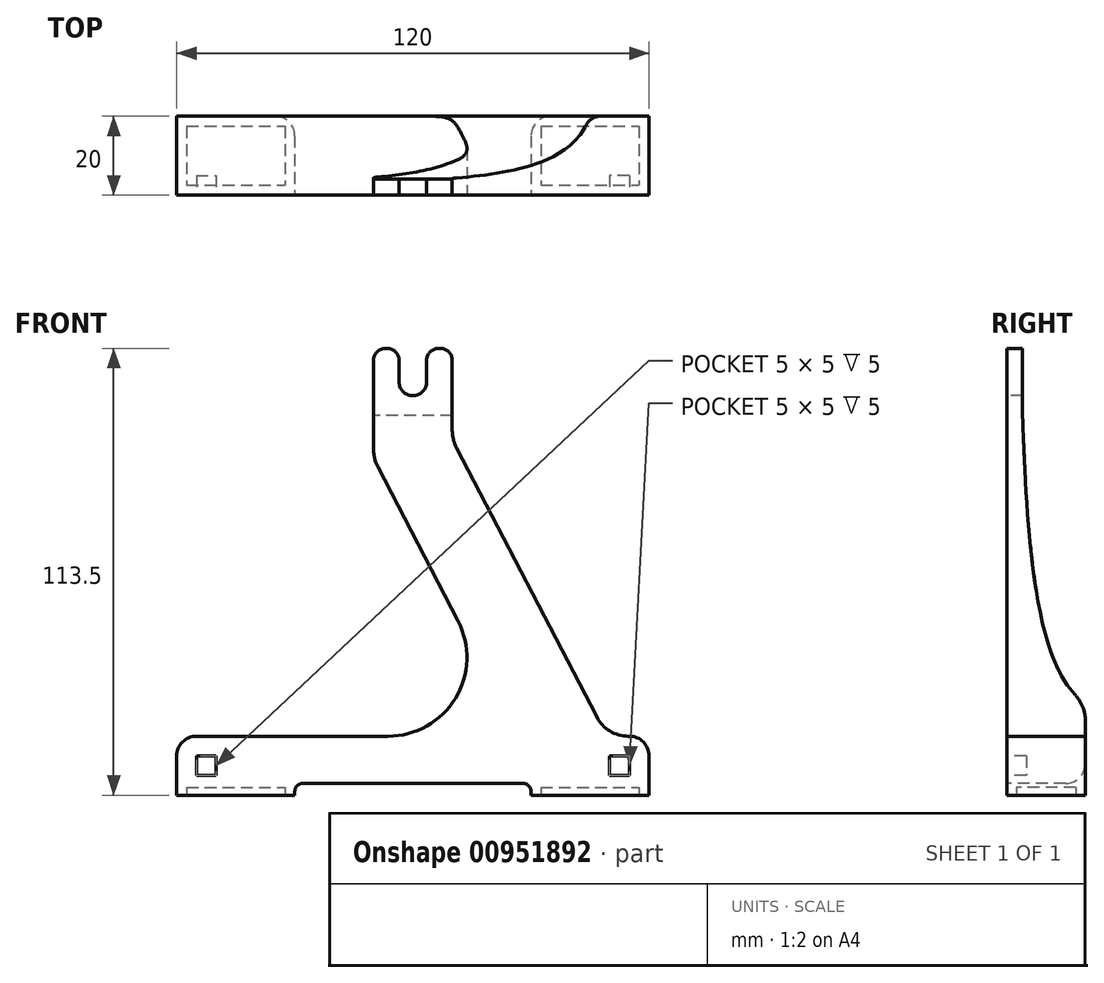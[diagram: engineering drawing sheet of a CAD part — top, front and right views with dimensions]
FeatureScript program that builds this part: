
annotation { "Feature Type Name" : "Feature", "Feature Type Description" : "" }
export const myFeature = defineFeature(function(context is Context, id is Id, definition is map)
    precondition{}
    {
        {
            var Q0;
            Q0=qCreatedBy(makeId("Front.planeOp"),FACE);
            var sketch = newSketch(context, id + "F0", { "sketchPlane" : qUnion([Q0])});
            skArc(sketch, "E0", {"start": v(-3.5, 105) * mm, "mid": v(0, 101.5) * mm, "end": v(3.5, 105) * mm});
            skCircle(sketch, "E1", {"center": v(0, 105) * mm, "radius": 100 * mm, "construction": true});
            skLineSegment(sketch, "E2", {"start": v(-10, 110.5) * mm, "end": v(-10, 87.96) * mm});
            skLineSegment(sketch, "E3", {"start": v(-20, 15) * mm, "end": v(-55, 15) * mm});
            skLineSegment(sketch, "E4", {"start": v(-60, 10) * mm, "end": v(-60, 0) * mm});
            skLineSegment(sketch, "E5", {"start": v(-60, 0) * mm, "end": v(-30, 0) * mm});
            skLineSegment(sketch, "E6", {"start": v(-28, 3) * mm, "end": v(28, 3) * mm});
            skLineSegment(sketch, "E7", {"start": v(30, 0) * mm, "end": v(60, 0) * mm});
            skLineSegment(sketch, "E8", {"start": v(60, 0) * mm, "end": v(60, 10) * mm});
            skLineSegment(sketch, "E9", {"start": v(55, 15) * mm, "end": v(54.7, 15) * mm});
            skLineSegment(sketch, "E10", {"start": v(10, 92.85) * mm, "end": v(10, 110.5) * mm});
            skLineSegment(sketch, "E11", {"start": v(7, 113.5) * mm, "end": v(6.5, 113.5) * mm});
            skLineSegment(sketch, "E12", {"start": v(-30, 1) * mm, "end": v(-30, 0) * mm});
            skLineSegment(sketch, "E13", {"start": v(30, 1) * mm, "end": v(30, 0) * mm});
            skPoint(sketch, "E14.orphan", {"position": v(-45, 0) * mm});
            skPoint(sketch, "E15.orphan", {"position": v(45, 0) * mm});
            skPoint(sketch, "E16.visualSharp", {"position": v(-10, 15) * mm});
            skPoint(sketch, "E17.visualSharp", {"position": v(10, 15) * mm});
            skPoint(sketch, "E18.visualSharp", {"position": v(-10, 113.5) * mm});
            skArc(sketch, "E18.filletArc", {"start": v(-7, 113.5) * mm, "mid": v(-9.12, 112.62) * mm, "end": v(-10, 110.5) * mm});
            skPoint(sketch, "E19.visualSharp", {"position": v(10, 113.5) * mm});
            skArc(sketch, "E19.filletArc", {"start": v(10, 110.5) * mm, "mid": v(9.12, 112.62) * mm, "end": v(7, 113.5) * mm});
            skPoint(sketch, "E20.visualSharp", {"position": v(-60, 15) * mm});
            skArc(sketch, "E20.filletArc", {"start": v(-55, 15) * mm, "mid": v(-58.54, 13.54) * mm, "end": v(-60, 10) * mm});
            skPoint(sketch, "E21.visualSharp", {"position": v(60, 15) * mm});
            skArc(sketch, "E21.filletArc", {"start": v(60, 10) * mm, "mid": v(58.54, 13.54) * mm, "end": v(55, 15) * mm});
            skPoint(sketch, "E22.visualSharp", {"position": v(30, 3) * mm});
            skArc(sketch, "E22.filletArc", {"start": v(30, 1) * mm, "mid": v(29.41, 2.41) * mm, "end": v(28, 3) * mm});
            skPoint(sketch, "E23.visualSharp", {"position": v(-30, 3) * mm});
            skArc(sketch, "E23.filletArc", {"start": v(-28, 3) * mm, "mid": v(-29.41, 2.41) * mm, "end": v(-30, 1) * mm});
            skLineSegment(sketch, "E24", {"start": v(-3.5, 105) * mm, "end": v(-3.5, 110.5) * mm});
            skLineSegment(sketch, "E25", {"start": v(3.5, 105) * mm, "end": v(3.5, 110.5) * mm});
            skLineSegment(sketch, "E26.trimOffspring", {"start": v(-6.5, 113.5) * mm, "end": v(-7, 113.5) * mm});
            skPoint(sketch, "E27.visualSharp", {"position": v(-3.5, 113.5) * mm});
            skArc(sketch, "E27.filletArc", {"start": v(-3.5, 110.5) * mm, "mid": v(-4.38, 112.62) * mm, "end": v(-6.5, 113.5) * mm});
            skPoint(sketch, "E28.visualSharp", {"position": v(3.5, 113.5) * mm});
            skArc(sketch, "E28.filletArc", {"start": v(6.5, 113.5) * mm, "mid": v(4.38, 112.62) * mm, "end": v(3.5, 110.5) * mm});
            skLineSegment(sketch, "E29", {"start": v(11.13, 88.23) * mm, "end": v(46.72, 19.85) * mm});
            skLineSegment(sketch, "E30", {"start": v(-8.87, 83.34) * mm, "end": v(11.48, 44.23) * mm});
            skLineSegment(sketch, "E31.trimOffspring", {"start": v(-6.26, 15) * mm, "end": v(-20, 15) * mm});
            skPoint(sketch, "E32.visualSharp", {"position": v(-10, 85.5) * mm});
            skArc(sketch, "E32.filletArc", {"start": v(-10, 87.96) * mm, "mid": v(-9.71, 85.58) * mm, "end": v(-8.87, 83.34) * mm});
            skPoint(sketch, "E33.visualSharp", {"position": v(10, 90.4) * mm});
            skArc(sketch, "E33.filletArc", {"start": v(10, 92.85) * mm, "mid": v(10.29, 90.47) * mm, "end": v(11.13, 88.23) * mm});
            skPoint(sketch, "E34.visualSharp", {"position": v(49.24, 15) * mm});
            skArc(sketch, "E34.filletArc", {"start": v(46.72, 19.85) * mm, "mid": v(50.03, 16.3) * mm, "end": v(54.7, 15) * mm});
            skPoint(sketch, "E35.visualSharp", {"position": v(26.7, 15) * mm});
            skArc(sketch, "E35.filletArc", {"start": v(-6.26, 15) * mm, "mid": v(10.84, 24.62) * mm, "end": v(11.48, 44.23) * mm});
            skSolve(sketch);
        }
        {
            var Q0;
            Q0=makeQuery(id+"F0.imprint","IMPRINT",FACE,{"disambiguationData":[TD([[makeQuery(id+"F0.imprint","IMPRINT",EDGE,{"derivedFrom":sQuery(id+"F0.wireOp",EDGE,"E0")}),-1.0]])]});
            extrude(context, id + "F1", {"entities" : qUnion([Q0]), "depth" : 20 * mm, "offsetDistance" : 25 * mm});
        }
        {
            var Q0;
            Q0=makeQuery(id+"F1.opExtrude","SWEPT_FACE",FACE,{"disambiguationData":[OSD([sQuery(id+"F0.wireOp",EDGE,"E10")])]});
            var sketch = newSketch(context, id + "F2", { "sketchPlane" : qUnion([Q0])});
            skLineSegment(sketch, "E36", {"start": v(-4, 116.6) * mm, "end": v(-4, 96.5) * mm});
            skLineSegment(sketch, "E37", {"start": v(-20, 116.6) * mm, "end": v(-4, 116.6) * mm});
            skPoint(sketch, "E38.visualSharp", {"position": v(-4, 88.5) * mm});
            skLineSegment(sketch, "E39", {"start": v(-25.17, 79.44) * mm, "end": v(-25.17, 116.6) * mm});
            skLineSegment(sketch, "E40", {"start": v(-25.17, 116.6) * mm, "end": v(-20, 116.6) * mm});
            skPoint(sketch, "E41.visualSharp", {"position": v(-20, 88.5) * mm});
            skFitSpline(sketch, "E42", {"points": [v(-4, 96.5) * mm, v(-13.32, 31.43) * mm, v(-22.33, 23.5) * mm, v(-25.17, 79.44) * mm], "startDerivative": vector(-7.01, -189.31) * mm, "endDerivative": vector(0.02, 210.5) * mm});
            skSolve(sketch);
        }
        {
            var Q0;
            Q0=makeQuery(id+"F1.opExtrude","SWEPT_FACE",FACE,{"disambiguationData":[OSD([sQuery(id+"F0.wireOp",EDGE,"E5")])]});
            var sketch = newSketch(context, id + "F3", { "sketchPlane" : qUnion([Q0])});
            skLineSegment(sketch, "E43.bottom", {"start": v(-57.5, 17.5) * mm, "end": v(-32.5, 17.5) * mm});
            skLineSegment(sketch, "E43.top", {"start": v(-57.5, 2.5) * mm, "end": v(-32.5, 2.5) * mm});
            skLineSegment(sketch, "E43.left", {"start": v(-57.5, 17.5) * mm, "end": v(-57.5, 2.5) * mm});
            skLineSegment(sketch, "E43.right", {"start": v(-32.5, 17.5) * mm, "end": v(-32.5, 2.5) * mm});
            skLineSegment(sketch, "E44.bottom", {"start": v(32.5, 17.5) * mm, "end": v(57.5, 17.5) * mm});
            skLineSegment(sketch, "E44.top", {"start": v(32.5, 2.5) * mm, "end": v(57.5, 2.5) * mm});
            skLineSegment(sketch, "E44.left", {"start": v(32.5, 17.5) * mm, "end": v(32.5, 2.5) * mm});
            skLineSegment(sketch, "E44.right", {"start": v(57.5, 17.5) * mm, "end": v(57.5, 2.5) * mm});
            skSolve(sketch);
        }
        {
            var Q0;
            Q0=makeQuery(id+"F3.imprint","IMPRINT",FACE,{"disambiguationData":[TD([[makeQuery(id+"F3.imprint","IMPRINT",EDGE,{"derivedFrom":sQuery(id+"F3.wireOp",EDGE,"E43.bottom")}),-1.0]])]});
            var Q1;
            Q1=makeQuery(id+"F3.imprint","IMPRINT",FACE,{"disambiguationData":[TD([[makeQuery(id+"F3.imprint","IMPRINT",EDGE,{"derivedFrom":sQuery(id+"F3.wireOp",EDGE,"E44.bottom")}),-1.0]])]});
            extrude(context, id + "F4", {"entities" : qUnion([Q0, Q1]), "operationType" : NewBodyOperationType.REMOVE, "oppositeDirection" : true, "depth" : 2 * mm, "offsetDistance" : 25 * mm});
        }
        {
            var Q0;
            {var subQ1=sQuery(id+"F2.wireOp",EDGE,"E37");Q0=makeQuery(id+"F2.imprint","IMPRINT",FACE,{"disambiguationData":[TD([[makeQuery(id+"F2.imprint","IMPRINT",EDGE,{"derivedFrom":subQ1}),-1.0]])]});}
            var Q1;
            {var subQ0=sQuery(id+"F0.wireOp",EDGE,"E10");var subQ1=makeQuery(id+"F1.opExtrude","CAP_EDGE",EDGE,{"disambiguationData":[OSD([subQ0])],"isStart":false});Q1=makeQuery(id+"F2.imprint","IMPRINT",FACE,{"disambiguationData":[TD([[makeQuery(id+"F2.imprint","IMPRINT",EDGE,{"derivedFrom":subQ1}),-1.0]])]});}
            extrude(context, id + "F5", {"entities" : qUnion([Q0, Q1]), "operationType" : NewBodyOperationType.REMOVE, "depth" : 75 * mm, "offsetDistance" : 25 * mm, "symmetric" : true});
        }
        {
            var Q0;
            Q0=makeQuery(id+"F5.boolean.opBoolean","INTERSECT",EDGE,{"derivedFrom":[makeQuery(id+"F1.opExtrude","CAP_FACE",FACE,{"disambiguationData":[OSD([sQuery(id+"F0.wireOp",EDGE,"E0"),sQuery(id+"F0.wireOp",EDGE,"E2"),sQuery(id+"F0.wireOp",EDGE,"E3"),sQuery(id+"F0.wireOp",EDGE,"E4"),sQuery(id+"F0.wireOp",EDGE,"E5"),sQuery(id+"F0.wireOp",EDGE,"E6"),sQuery(id+"F0.wireOp",EDGE,"E7"),sQuery(id+"F0.wireOp",EDGE,"E8"),sQuery(id+"F0.wireOp",EDGE,"E9"),sQuery(id+"F0.wireOp",EDGE,"E10"),sQuery(id+"F0.wireOp",EDGE,"E11"),sQuery(id+"F0.wireOp",EDGE,"E12"),sQuery(id+"F0.wireOp",EDGE,"E13"),sQuery(id+"F0.wireOp",EDGE,"E18.filletArc"),sQuery(id+"F0.wireOp",EDGE,"E19.filletArc"),sQuery(id+"F0.wireOp",EDGE,"E20.filletArc"),sQuery(id+"F0.wireOp",EDGE,"E21.filletArc"),sQuery(id+"F0.wireOp",EDGE,"E22.filletArc"),sQuery(id+"F0.wireOp",EDGE,"E23.filletArc"),sQuery(id+"F0.wireOp",EDGE,"E24"),sQuery(id+"F0.wireOp",EDGE,"E25"),sQuery(id+"F0.wireOp",EDGE,"E26.trimOffspring"),sQuery(id+"F0.wireOp",EDGE,"E27.filletArc"),sQuery(id+"F0.wireOp",EDGE,"E28.filletArc"),sQuery(id+"F0.wireOp",EDGE,"E29"),sQuery(id+"F0.wireOp",EDGE,"E30"),sQuery(id+"F0.wireOp",EDGE,"E31.trimOffspring"),sQuery(id+"F0.wireOp",EDGE,"E32.filletArc"),sQuery(id+"F0.wireOp",EDGE,"E33.filletArc"),sQuery(id+"F0.wireOp",EDGE,"E34.filletArc"),sQuery(id+"F0.wireOp",EDGE,"E35.filletArc")])],"isStart":false}),makeQuery(id+"F5.opExtrude","SWEPT_FACE",FACE,{"disambiguationData":[OSD([sQuery(id+"F2.wireOp",EDGE,"E42")])]})]});
            fillet(context, id + "F6", {"entities" : qUnion([Q0]), "radius" : 10 * mm, "tangentPropagation" : true, "allowEdgeOverflow" : false});
        }
        {
            var Q0;
            Q0=makeQuery(id+"F1.opExtrude","CAP_EDGE",EDGE,{"disambiguationData":[OSD([sQuery(id+"F0.wireOp",EDGE,"E6")])],"isStart":false});
            fillet(context, id + "F7", {"entities" : qUnion([Q0]), "radius" : 5 * mm, "tangentPropagation" : true, "allowEdgeOverflow" : false});
        }
        {
            var Q0;
            Q0=makeQuery(id+"F0.imprint","IMPRINT",FACE,{"disambiguationData":[TD([[makeQuery(id+"F0.imprint","IMPRINT",EDGE,{"derivedFrom":sQuery(id+"F0.wireOp",EDGE,"E0")}),-1.0]])]});
            var sketch = newSketch(context, id + "F8", { "sketchPlane" : qUnion([Q0])});
            skLineSegment(sketch, "E45.bottom", {"start": v(55, 10) * mm, "end": v(50, 10) * mm});
            skLineSegment(sketch, "E45.top", {"start": v(55, 5) * mm, "end": v(50, 5) * mm});
            skLineSegment(sketch, "E45.left", {"start": v(55, 10) * mm, "end": v(55, 5) * mm});
            skLineSegment(sketch, "E45.right", {"start": v(50, 10) * mm, "end": v(50, 5) * mm});
            skLineSegment(sketch, "E46.bottom", {"start": v(-55, 10) * mm, "end": v(-50, 10) * mm});
            skLineSegment(sketch, "E46.top", {"start": v(-55, 5) * mm, "end": v(-50, 5) * mm});
            skLineSegment(sketch, "E46.left", {"start": v(-55, 10) * mm, "end": v(-55, 5) * mm});
            skLineSegment(sketch, "E46.right", {"start": v(-50, 10) * mm, "end": v(-50, 5) * mm});
            skSolve(sketch);
        }
        {
            var Q0;
            Q0=makeQuery(id+"F8.imprint","IMPRINT",FACE,{"disambiguationData":[TD([[makeQuery(id+"F8.imprint","IMPRINT",EDGE,{"derivedFrom":sQuery(id+"F8.wireOp",EDGE,"E45.bottom")}),1.0]])]});
            var Q1;
            Q1=makeQuery(id+"F8.imprint","IMPRINT",FACE,{"disambiguationData":[TD([[makeQuery(id+"F8.imprint","IMPRINT",EDGE,{"derivedFrom":sQuery(id+"F8.wireOp",EDGE,"E46.bottom")}),-1.0]])]});
            extrude(context, id + "F9", {"entities" : qUnion([Q0, Q1]), "operationType" : NewBodyOperationType.REMOVE, "depth" : 5 * mm, "offsetDistance" : 25 * mm});
        }
        {
            var Q0;
            Q0=qCreatedBy(makeId("Front.planeOp"),FACE);
            cPlane(context, id + "F10", {"entities" : qUnion([Q0]), "cplaneType" : CPlaneType.OFFSET, "offset" : 25 * mm, "oppositeDirection" : true, "width" : 150 * mm, "height" : 150 * mm});
        }
        {
            var Q0;
            Q0=makeQuery(id+"F1.opExtrude","SWEPT_BODY",BODY,{"disambiguationData":[OSD([sQuery(id+"F0.wireOp",EDGE,"E0"),sQuery(id+"F0.wireOp",EDGE,"E2"),sQuery(id+"F0.wireOp",EDGE,"E3"),sQuery(id+"F0.wireOp",EDGE,"E4"),sQuery(id+"F0.wireOp",EDGE,"E5"),sQuery(id+"F0.wireOp",EDGE,"E6"),sQuery(id+"F0.wireOp",EDGE,"E7"),sQuery(id+"F0.wireOp",EDGE,"E8"),sQuery(id+"F0.wireOp",EDGE,"E9"),sQuery(id+"F0.wireOp",EDGE,"E10"),sQuery(id+"F0.wireOp",EDGE,"E11"),sQuery(id+"F0.wireOp",EDGE,"E12"),sQuery(id+"F0.wireOp",EDGE,"E13"),sQuery(id+"F0.wireOp",EDGE,"E18.filletArc"),sQuery(id+"F0.wireOp",EDGE,"E19.filletArc"),sQuery(id+"F0.wireOp",EDGE,"E20.filletArc"),sQuery(id+"F0.wireOp",EDGE,"E21.filletArc"),sQuery(id+"F0.wireOp",EDGE,"E22.filletArc"),sQuery(id+"F0.wireOp",EDGE,"E23.filletArc"),sQuery(id+"F0.wireOp",EDGE,"E24"),sQuery(id+"F0.wireOp",EDGE,"E25"),sQuery(id+"F0.wireOp",EDGE,"E26.trimOffspring"),sQuery(id+"F0.wireOp",EDGE,"E27.filletArc"),sQuery(id+"F0.wireOp",EDGE,"E28.filletArc"),sQuery(id+"F0.wireOp",EDGE,"E29"),sQuery(id+"F0.wireOp",EDGE,"E30"),sQuery(id+"F0.wireOp",EDGE,"E31.trimOffspring"),sQuery(id+"F0.wireOp",EDGE,"E32.filletArc"),sQuery(id+"F0.wireOp",EDGE,"E33.filletArc"),sQuery(id+"F0.wireOp",EDGE,"E34.filletArc"),sQuery(id+"F0.wireOp",EDGE,"E35.filletArc")])]});
            var Q1;
            Q1=qCreatedBy(id+"F10.planeOp",FACE);
            mirror(context, id + "F11", {"entities" : qUnion([Q0]), "mirrorPlane" : qUnion([Q1])});
        }
        {
            var Q0;
            Q0=makeQuery(id+"F1.opExtrude","SWEPT_BODY",BODY,{"disambiguationData":[OSD([sQuery(id+"F0.wireOp",EDGE,"E0"),sQuery(id+"F0.wireOp",EDGE,"E2"),sQuery(id+"F0.wireOp",EDGE,"E3"),sQuery(id+"F0.wireOp",EDGE,"E4"),sQuery(id+"F0.wireOp",EDGE,"E5"),sQuery(id+"F0.wireOp",EDGE,"E6"),sQuery(id+"F0.wireOp",EDGE,"E7"),sQuery(id+"F0.wireOp",EDGE,"E8"),sQuery(id+"F0.wireOp",EDGE,"E9"),sQuery(id+"F0.wireOp",EDGE,"E10"),sQuery(id+"F0.wireOp",EDGE,"E11"),sQuery(id+"F0.wireOp",EDGE,"E12"),sQuery(id+"F0.wireOp",EDGE,"E13"),sQuery(id+"F0.wireOp",EDGE,"E18.filletArc"),sQuery(id+"F0.wireOp",EDGE,"E19.filletArc"),sQuery(id+"F0.wireOp",EDGE,"E20.filletArc"),sQuery(id+"F0.wireOp",EDGE,"E21.filletArc"),sQuery(id+"F0.wireOp",EDGE,"E22.filletArc"),sQuery(id+"F0.wireOp",EDGE,"E23.filletArc"),sQuery(id+"F0.wireOp",EDGE,"E24"),sQuery(id+"F0.wireOp",EDGE,"E25"),sQuery(id+"F0.wireOp",EDGE,"E26.trimOffspring"),sQuery(id+"F0.wireOp",EDGE,"E27.filletArc"),sQuery(id+"F0.wireOp",EDGE,"E28.filletArc"),sQuery(id+"F0.wireOp",EDGE,"E29"),sQuery(id+"F0.wireOp",EDGE,"E30"),sQuery(id+"F0.wireOp",EDGE,"E31.trimOffspring"),sQuery(id+"F0.wireOp",EDGE,"E32.filletArc"),sQuery(id+"F0.wireOp",EDGE,"E33.filletArc"),sQuery(id+"F0.wireOp",EDGE,"E34.filletArc"),sQuery(id+"F0.wireOp",EDGE,"E35.filletArc")])]});
            deleteBodies(context, id + "F12", {"entities" : qUnion([Q0])});
        }
    });
